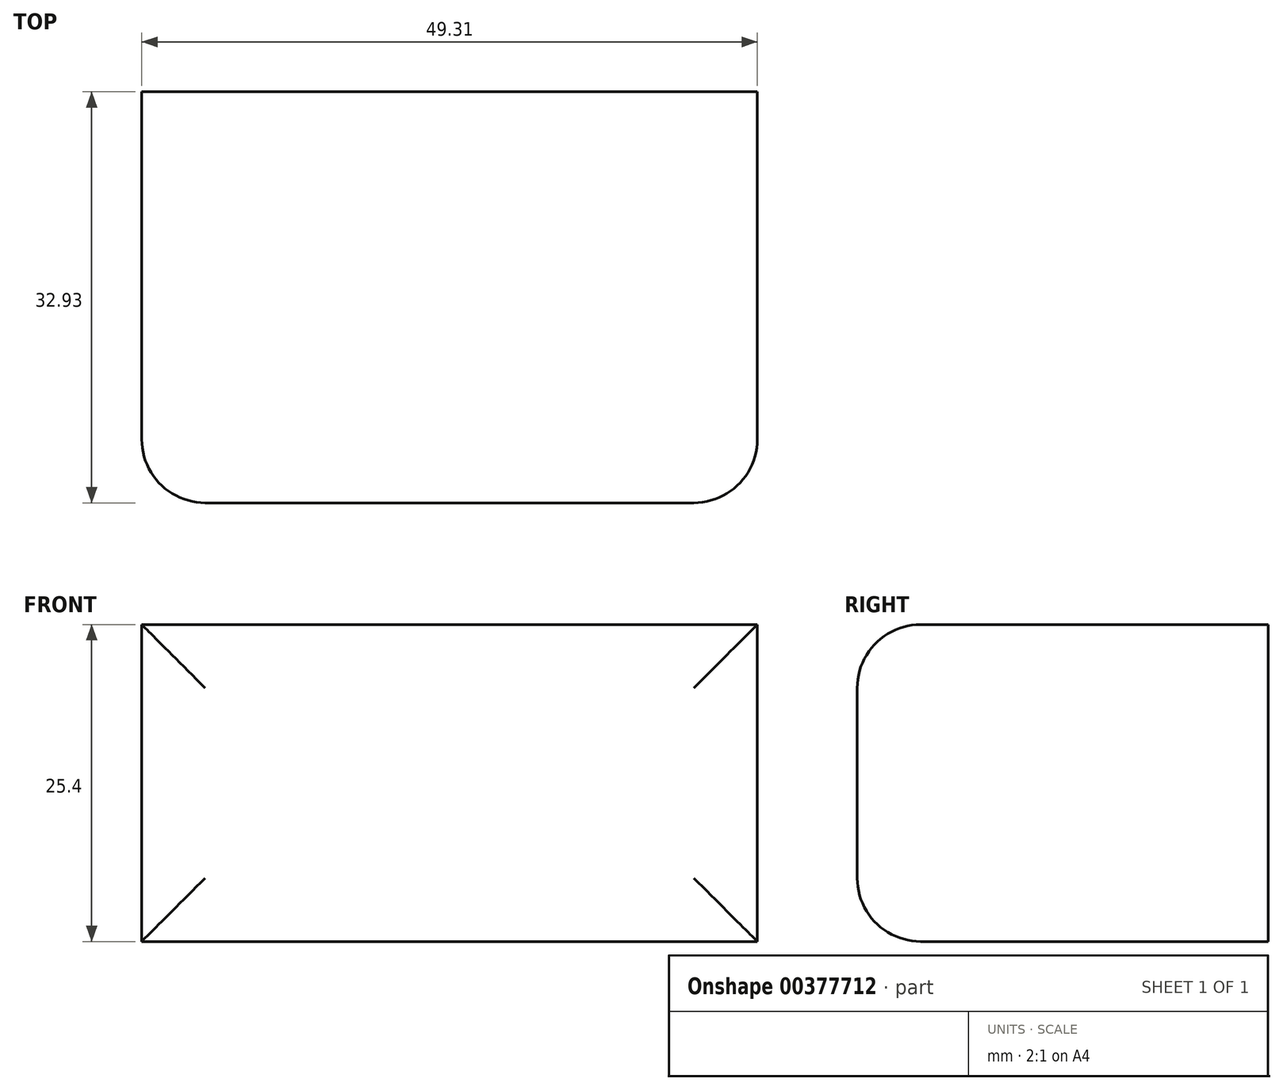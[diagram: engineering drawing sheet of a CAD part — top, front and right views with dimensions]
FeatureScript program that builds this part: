
annotation { "Feature Type Name" : "Feature", "Feature Type Description" : "" }
export const myFeature = defineFeature(function(context is Context, id is Id, definition is map)
    precondition{}
    {
        {
            var Q0;
            Q0=qCreatedBy(makeId("Top.planeOp"),FACE);
            var sketch = newSketch(context, id + "F0", { "sketchPlane" : qUnion([Q0])});
            skLineSegment(sketch, "E0.bottom", {"start": v(-24.25, 16.78) * mm, "end": v(25.06, 16.78) * mm});
            skLineSegment(sketch, "E0.top", {"start": v(-24.25, -16.15) * mm, "end": v(25.06, -16.15) * mm});
            skLineSegment(sketch, "E0.left", {"start": v(-24.25, 16.78) * mm, "end": v(-24.25, -16.15) * mm});
            skLineSegment(sketch, "E0.right", {"start": v(25.06, 16.78) * mm, "end": v(25.06, -16.15) * mm});
            skSolve(sketch);
        }
        {
            var Q0;
            Q0=makeQuery(id+"F0.imprint","IMPRINT",FACE,{"disambiguationData":[TD([[makeQuery(id+"F0.imprint","IMPRINT",EDGE,{"derivedFrom":sQuery(id+"F0.wireOp",EDGE,"E0.bottom")}),-1.0]])]});
            extrude(context, id + "F1", {"entities" : qUnion([Q0]), "depth" : 25.4 * mm});
        }
        {
            var Q0;
            Q0=makeQuery(id+"F1.opExtrude","SWEPT_FACE",FACE,{"disambiguationData":[OSD([sQuery(id+"F0.wireOp",EDGE,"E0.top")])]});
            fillet(context, id + "F2", {"entities" : qUnion([Q0]), "radius" : 5.08 * mm, "tangentPropagation" : true, "allowEdgeOverflow" : false});
        }
    });
